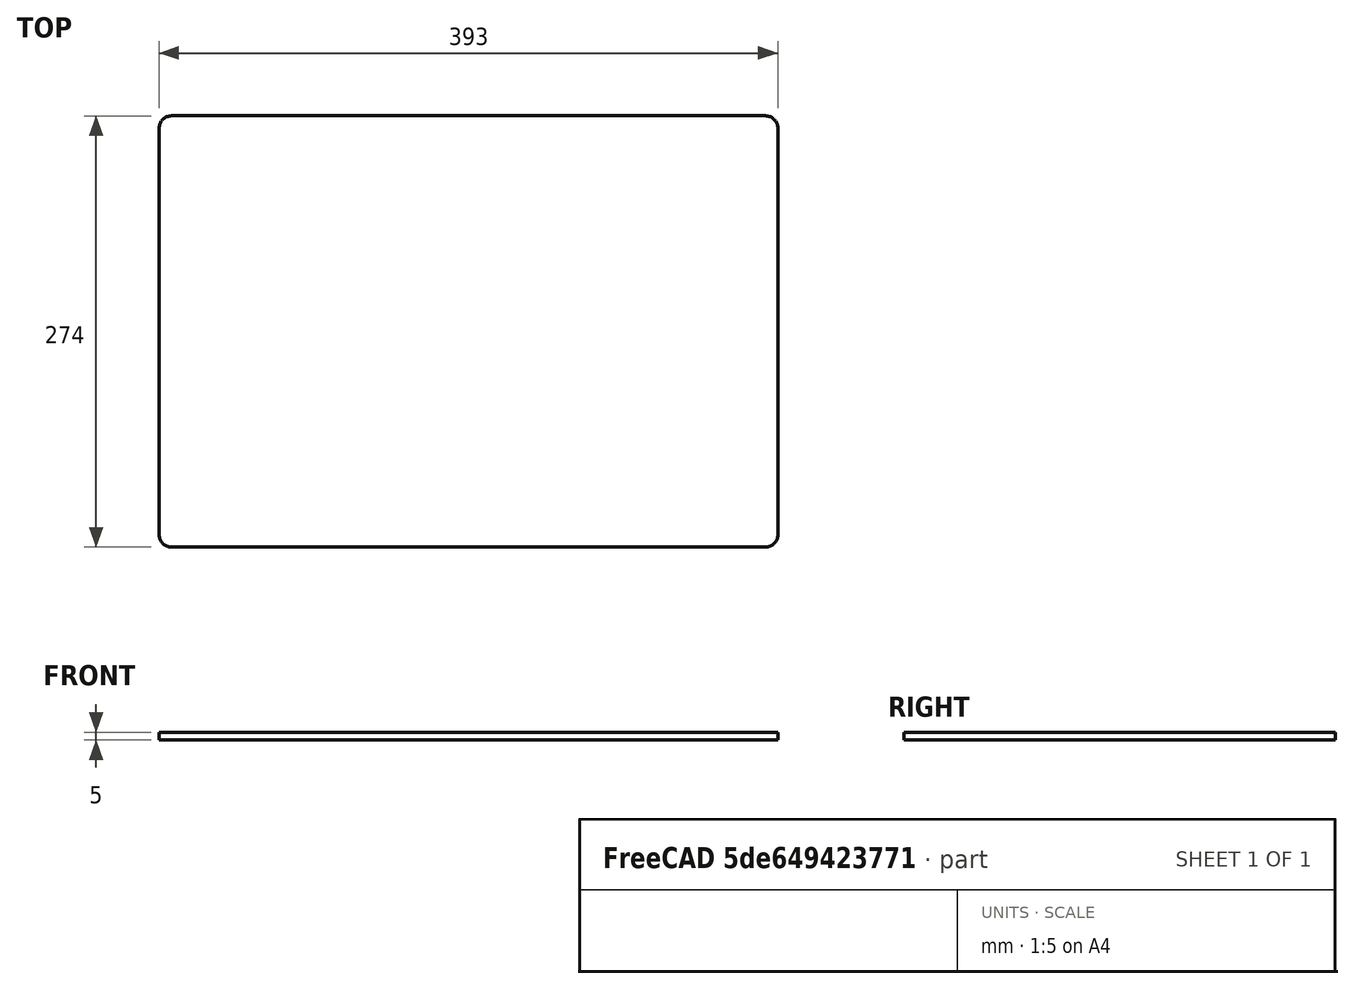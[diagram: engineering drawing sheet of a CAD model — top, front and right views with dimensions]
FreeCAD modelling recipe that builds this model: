
FCSTD DOCUMENT  (FreeCAD 0.19R24366 (Git))
Label: solarpanel_Voltaic17watt18volt
License: All rights reserved
LicenseURL: http://en.wikipedia.org/wiki/All_rights_reserved
objects: App::Part×1, Sketcher::SketchObject×1, PartDesign::Pad×1, PartDesign::Body×1
note: 4 computed .brp shape members not serialized (recipe doc carries the construction recipe); baked Part::Feature solids carry a one-line shape summary decoded from their .brp

FEATURE [App::Part] Part  label="SolarPanelVoltaic17Watt18Volt"
  Origin = -> Origin
FEATURE [Sketcher::SketchObject] Sketch
  FullyConstrained = false
  MapMode = 5
  Support = -> [XY_Plane001]
  sketch-geometry (8):
    g0: LineSegment StartX=-145.309 StartY=103.402 StartZ=0 EndX=231.838 EndY=103.402 EndZ=0
    g1: LineSegment StartX=239.764 StartY=95.4761 StartZ=0 EndX=239.764 EndY=-162.671 EndZ=0
    g2: LineSegment StartX=231.838 StartY=-170.598 StartZ=0 EndX=-145.309 EndY=-170.598 EndZ=0
    g3: LineSegment StartX=-153.236 StartY=-162.671 StartZ=0 EndX=-153.236 EndY=95.4761 EndZ=0
    g4: ArcOfCircle CenterX=-145.309 CenterY=95.4761 CenterZ=0 NormalX=0 NormalY=0 NormalZ=1 AngleXU=0 Radius=7.9263 StartAngle=1.5708 EndAngle=3.14159
    g5: ArcOfCircle CenterX=-145.309 CenterY=-162.671 CenterZ=0 NormalX=0 NormalY=0 NormalZ=1 AngleXU=0 Radius=7.9263 StartAngle=3.14159 EndAngle=4.71239
    g6: ArcOfCircle CenterX=231.838 CenterY=-162.671 CenterZ=0 NormalX=0 NormalY=0 NormalZ=1 AngleXU=0 Radius=7.9263 StartAngle=4.71239 EndAngle=6.28319
    g7: ArcOfCircle CenterX=231.838 CenterY=95.4761 CenterZ=0 NormalX=0 NormalY=0 NormalZ=1 AngleXU=0 Radius=7.9263 StartAngle=2e-16 EndAngle=1.5708
  constraints (17):
    c: Horizontal(g0)
    c: Horizontal(g2)
    c: Vertical(g1)
    c: Vertical(g3)
    c: Tangent(g3,g4) = 1.5708
    c: Tangent(g0,g4) = 1.5708
    c: Tangent(g3,g5) = 1.5708
    c: Tangent(g2,g5) = 1.5708
    c: Tangent(g2,g6) = 1.5708
    c: Tangent(g1,g6) = 1.5708
    c: Tangent(g0,g7) = 1.5708
    c: Tangent(g1,g7) = 1.5708
    c: Horizontal(g7,g4)
    c: Vertical(g5,g4)
    c: Vertical(g7,g6)
    c: DistanceY(g2,g0) = 274
    c: DistanceX(g3,g1) = 393
FEATURE [PartDesign::Pad] Pad
  Direction = (0,0,1)
  Length = 5
  Length2 = 100
  Profile = -> Sketch
  Type = 0
  UseCustomVector = true
FEATURE [PartDesign::Body] Body
  Group = -> [Sketch,Pad]
  Origin = -> Origin001
  Tip = -> Pad
